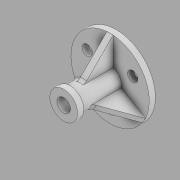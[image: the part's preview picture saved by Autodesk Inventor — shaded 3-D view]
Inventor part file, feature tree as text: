
AUTODESK INVENTOR PART (.ipt)
format: ipt  version: 2020 (Build 240168000, 168)  size: 207,360 bytes
history: native  units: mm
features: sketch x7, other x4, extrude x3, plane x2, hole x1, fillet x1
ambient origin geometry x8: Origin, YZ Plane, XZ Plane, XY Plane, X Axis, Y Axis, Z Axis, Center Point
bodies: Body1 (feature_tree)
feature tree (18):
  other  "Sólido1"
  extrude  "Extrusión1"  Depth=102.0mm
  extrude  "Extrusión2"  Depth=20.0mm
  extrude  "Extrusión3"  Depth=12.0mm TaperAngle=0.0deg
  other  "Nervio1"
  plane  "Plano de trabajo2"
  plane  "Plano de trabajo3"
  other  "Nervio3"
  other  "Nervio4"
  hole  "Agujero1"  [1 undecoded]
  fillet  "Empalme1"  Radius=54.0mm
  sketch  "Boceto1"  dims[d0=152.0mm d1=102.0mm]
  sketch  "Boceto2"  dims[d3=30.0deg d4=20.0mm]
  sketch  "Boceto3"  dims[d5=30.0mm d7=360.0deg d9=12.0mm d10=0.0mm]
  sketch  "Boceto4"  dims[d11=44.0mm d12=78.0mm d13=0.0mm d14=54.0mm]
  sketch  "Boceto6"  dims[d15=12.0mm d16=0.0mm]
  sketch  "Boceto7"  dims[d17=45.0deg]
  sketch  "Boceto8"  dims[d18=1.0mm d19=12.0mm d20=0.0mm d21=0.0mm d22=1.0mm d23=1.0mm d33=120.0deg d34=60.0deg d35=45.0deg d36=1.0mm d37=12.0mm d38=0.0mm d39=0.0mm d40=1.0mm d41=1.0mm d42=45.0deg d43=1.0mm d44=12.0mm d45=0.0mm d46=0.0mm d47=1.0mm d48=1.0mm d49=26.0mm d50=6.0mm d51=4.0mm d52=2.0mm d53=90.0deg d54=8.0mm d55=20.594885mm d56=10.0mm]
note: 1 required parameter value undecoded (feature->parameter linkage not recoverable at this tier; creation-order binding heuristic only, values carry confidence <= 0.55)
